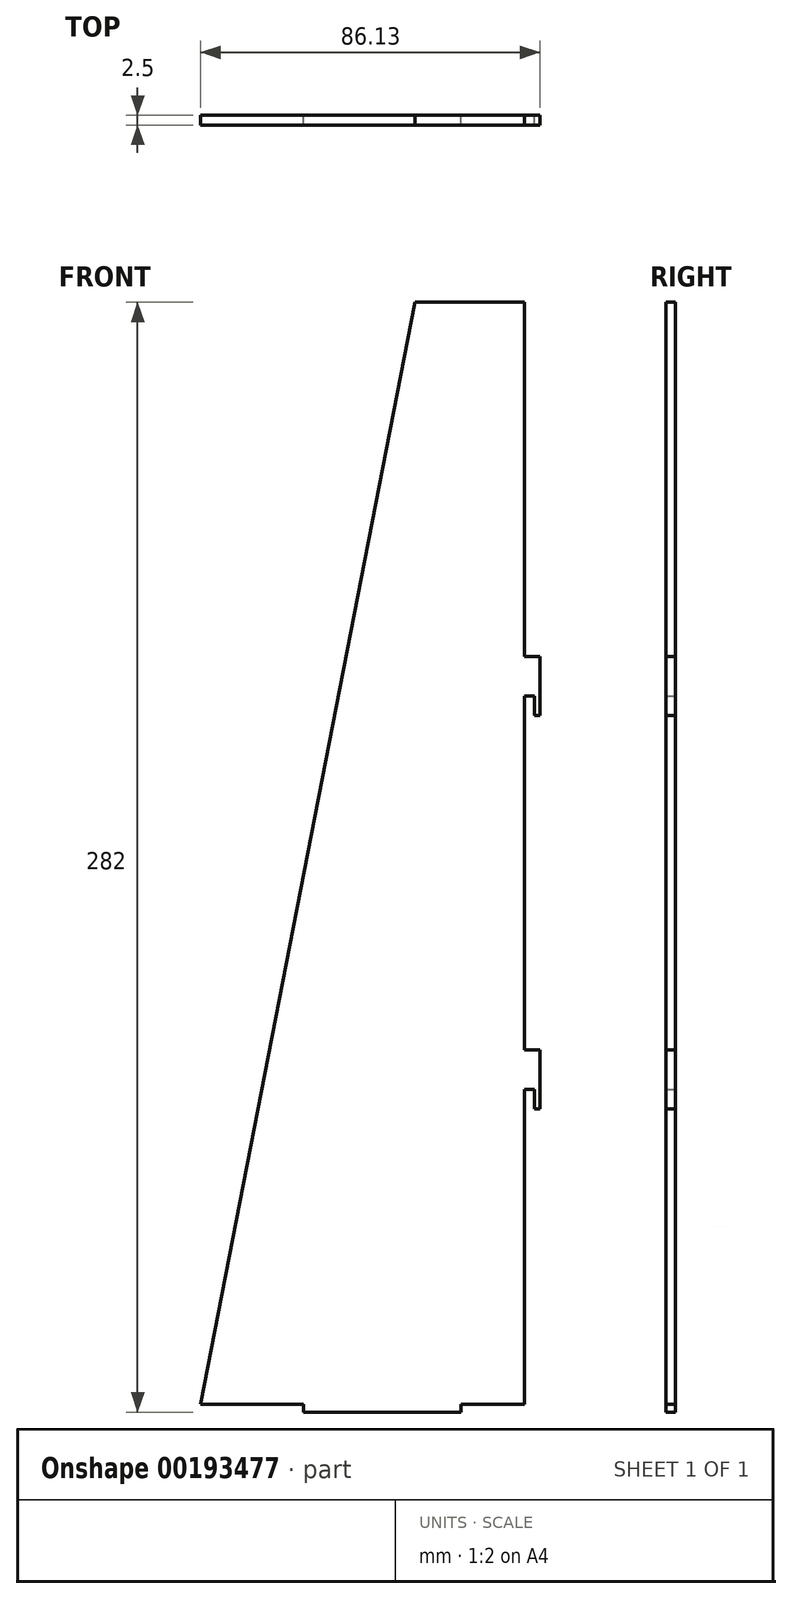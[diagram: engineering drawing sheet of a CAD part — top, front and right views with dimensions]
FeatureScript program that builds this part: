
annotation { "Feature Type Name" : "Feature", "Feature Type Description" : "" }
export const myFeature = defineFeature(function(context is Context, id is Id, definition is map)
    precondition{}
    {
        {
            var Q0;
            Q0=qCreatedBy(makeId("Front.planeOp"),FACE);
            var sketch = newSketch(context, id + "F0", { "sketchPlane" : qUnion([Q0])});
            skLineSegment(sketch, "E0", {"start": v(-86.13, 0) * mm, "end": v(-31.7, 280) * mm});
            skLineSegment(sketch, "E1", {"start": v(-31.7, 280) * mm, "end": v(0, 280) * mm});
            skLineSegment(sketch, "E2", {"start": v(0, 280) * mm, "end": v(0, 0) * mm});
            skLineSegment(sketch, "E3", {"start": v(0, 0) * mm, "end": v(-20, 0) * mm});
            skLineSegment(sketch, "E4", {"start": v(-60, 0) * mm, "end": v(-60, -2) * mm});
            skLineSegment(sketch, "E5", {"start": v(-60, -2) * mm, "end": v(-20, -2) * mm});
            skLineSegment(sketch, "E6", {"start": v(-20, -2) * mm, "end": v(-20, 0) * mm});
            skLineSegment(sketch, "E7.trimOffspring", {"start": v(-60, 0) * mm, "end": v(-86.13, 0) * mm});
            skSolve(sketch);
        }
        {
            var Q0;
            Q0=qSketchRegion(id+"F0",true);
            extrude(context, id + "F1", {"entities" : qUnion([Q0]), "depth" : 2.5 * mm});
        }
        {
            var Q0;
            Q0=qCreatedBy(makeId("Front.planeOp"),FACE);
            var sketch = newSketch(context, id + "F2", { "sketchPlane" : qUnion([Q0])});
            skLineSegment(sketch, "E8", {"start": v(25.52, 285.47) * mm, "end": v(-3.88, 285.47) * mm});
            skLineSegment(sketch, "E9", {"start": v(-3.88, 285.47) * mm, "end": v(-3.88, 190) * mm});
            skLineSegment(sketch, "E10", {"start": v(-3.88, 190) * mm, "end": v(3.67, 190) * mm});
            skLineSegment(sketch, "E11", {"start": v(3.67, 190) * mm, "end": v(3.67, 175) * mm});
            skLineSegment(sketch, "E12", {"start": v(3.67, 175) * mm, "end": v(-1.33, 175) * mm});
            skLineSegment(sketch, "E13", {"start": v(-1.33, 175) * mm, "end": v(-1.33, 180) * mm});
            skLineSegment(sketch, "E14", {"start": v(-1.33, 180) * mm, "end": v(-3.88, 180) * mm});
            skLineSegment(sketch, "E15", {"start": v(-3.88, 180) * mm, "end": v(-3.88, 90) * mm});
            skLineSegment(sketch, "E16.0.1.0", {"start": v(3.67, 90) * mm, "end": v(3.67, 75) * mm});
            skLineSegment(sketch, "E16.0.1.1", {"start": v(-3.88, 90) * mm, "end": v(3.67, 90) * mm});
            skLineSegment(sketch, "E16.0.1.2", {"start": v(3.67, 75) * mm, "end": v(-1.33, 75) * mm});
            skLineSegment(sketch, "E16.0.1.3", {"start": v(-1.33, 75) * mm, "end": v(-1.33, 80) * mm});
            skLineSegment(sketch, "E16.0.1.4", {"start": v(-1.33, 80) * mm, "end": v(-3.88, 80) * mm});
            skLineSegment(sketch, "E16.0.1.5", {"start": v(-3.88, 80) * mm, "end": v(-3.88, -10) * mm});
            skLineSegment(sketch, "E16.direction1", {"start": v(-1.33, 175) * mm, "end": v(23.67, 175) * mm, "construction": true});
            skLineSegment(sketch, "E16.direction2", {"start": v(-1.33, 175) * mm, "end": v(-1.33, 75) * mm, "construction": true});
            skLineSegment(sketch, "E17", {"start": v(-3.88, -10) * mm, "end": v(25.52, -10) * mm});
            skLineSegment(sketch, "E18", {"start": v(25.52, -10) * mm, "end": v(25.52, 285.47) * mm});
            skSolve(sketch);
        }
        {
            var Q0;
            Q0=qSketchRegion(id+"F2",true);
            extrude(context, id + "F3", {"entities" : qUnion([Q0]), "operationType" : NewBodyOperationType.REMOVE, "depth" : 25 * mm});
        }
    });
